# Revit family: Hinge_CI3400_Shut-It_DD-Technologies
name_source: partatom
category: Specialty Equipment
units: mm (PartAtom-declared; Revit-internal decimal feet)

## family parameters
Always vertical = Yes
Cut with Voids When Loaded = No
Enable Cutting in Views = No
Maintain Annotation Orientation = No
Part Type = Normal
Room Calculation Point = No
Round Connector Dimension = Use Diameter
Shared = No
Work Plane-Based = Yes

## types (1)
- CI3400 - Shut-It® Aluminum BadAss™
    Adjustable Total Length = 2.4-2.9” (61-74mm)
    Assembly Code = G2060.20 Fences and Gates
    Body Height = 1.75” (44mm)
    Body Width = 1.5” (38mm)
    Catalog Page = https://us.ddtech.com
    Color/Finish = Aluminum
    Default Elevation = 0 "
    Description = Aluminum hinge, weld-on, for flat post installation
    Gate Material = Aluminum
    Hinge Material = Aluminum
    Hinge Total Height = 3.8” (97mm)
    Horizontal Gap Adjustment (Variance) = 2-3⁄8” –  2-7⁄8” (61-74mm)
    Keynote = 32 31 00 Fence & Gates
    Load rating per gate*  (per pair of hinge) = 1,000 lb (450kg)
    Manufacturer = D&D Technologies
    Maximal Gate Weight*  (per pair of hinge) = 600 lb (270kg)
    Maximal Self-Closing Gate Weight*  (per pair of hinge) = Non Self-Closing
    Model = CI3400
    Product Name = Shut-It® Aluminum BadAss™
    Product Webpage with product image = https://us.ddtech.com
    Specification = https://us.ddtech.com
    Type = Hinge
    URL = https://ddtech.com
    Yoke Height = 2.8” (71mm)
    Yoke Thickness = 0.2” (5mm)
    Yoke Width = 1.5” (38mm)

## geometry (parser evidence)
native form markers: Sweep x8
no freeform markers — native parametric forms only
